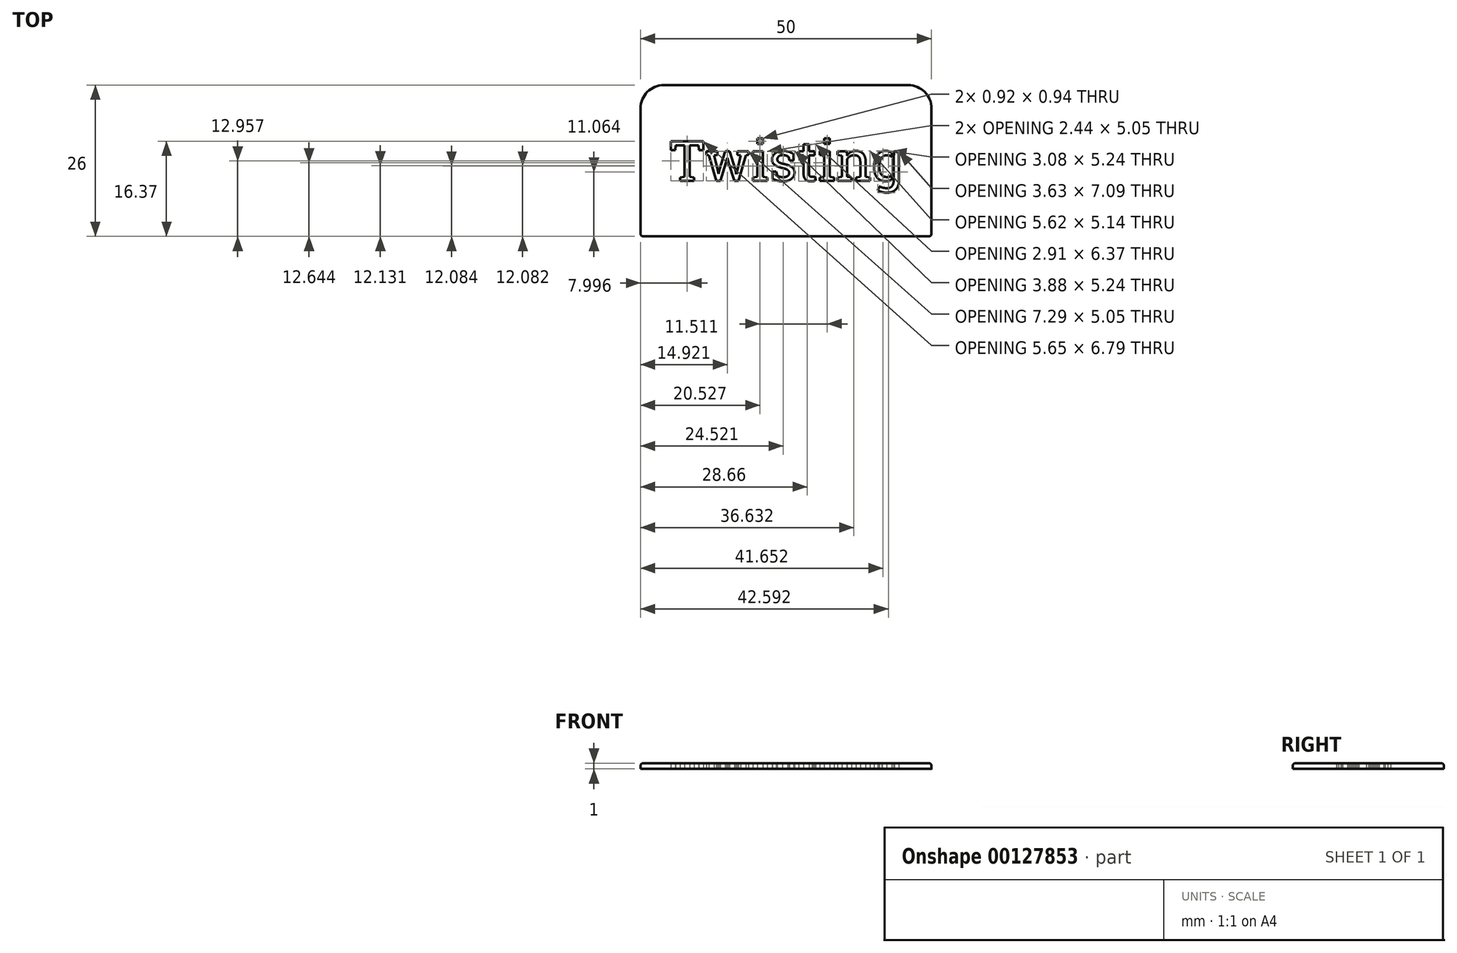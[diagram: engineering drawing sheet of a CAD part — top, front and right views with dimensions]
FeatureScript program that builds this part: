
annotation { "Feature Type Name" : "Feature", "Feature Type Description" : "" }
export const myFeature = defineFeature(function(context is Context, id is Id, definition is map)
    precondition{}
    {
        {
            var Q0;
            Q0=qCreatedBy(makeId("Top.planeOp"),FACE);
            var sketch = newSketch(context, id + "F0", { "sketchPlane" : qUnion([Q0])});
            skLineSegment(sketch, "E0.bottom", {"start": v(25, -13) * mm, "end": v(-25, -13) * mm});
            skLineSegment(sketch, "E0.top", {"start": v(21, 13) * mm, "end": v(-21, 13) * mm});
            skLineSegment(sketch, "E0.left", {"start": v(25, -13) * mm, "end": v(25, 9) * mm});
            skLineSegment(sketch, "E0.right", {"start": v(-25, -13) * mm, "end": v(-25, 9) * mm});
            skPoint(sketch, "E0.middle", {"position": v(0, 0) * mm});
            skPoint(sketch, "E1.visualSharp", {"position": v(-25, 13) * mm});
            skArc(sketch, "E1.filletArc", {"start": v(-21, 13) * mm, "mid": v(-23.83, 11.83) * mm, "end": v(-25, 9) * mm});
            skPoint(sketch, "E2.visualSharp", {"position": v(25, 13) * mm});
            skArc(sketch, "E2.filletArc", {"start": v(25, 9) * mm, "mid": v(23.83, 11.83) * mm, "end": v(21, 13) * mm});
            skText(sketch, "E3", { "text": "Twisting", "fontName": "RobotoSlab-Regular.ttf"});
            skLineSegment(sketch, "E4.bottom", {"start": v(18.5, 3.44) * mm, "end": v(18.2, 3.44) * mm});
            skLineSegment(sketch, "E4.top", {"start": v(18.5, -3.44) * mm, "end": v(18.2, -3.44) * mm});
            skLineSegment(sketch, "E4.left", {"start": v(18.5, 3.44) * mm, "end": v(18.5, -3.44) * mm});
            skLineSegment(sketch, "E4.right", {"start": v(18.2, 3.44) * mm, "end": v(18.2, -3.44) * mm});
            const initialGuessF0  = {"E3": [-0.02, -0.00344, 1, 0, 0.00688]};
            skSetInitialGuess(sketch, initialGuessF0);
            skSolve(sketch);
        }
        {
            var Q0;
            Q0=makeQuery(id+"F0.imprint","IMPRINT",FACE,{"disambiguationData":[TD([[makeQuery(id+"F0.imprint","IMPRINT",EDGE,{"derivedFrom":sQuery(id+"F0.wireOp",EDGE,"E0.bottom")}),-1.0]])]});
            var Q1;
            Q1=makeQuery(id+"F0.imprint","IMPRINT",FACE,{"disambiguationData":[TD([[makeQuery(id+"F0.imprint","IMPRINT",EDGE,{"derivedFrom":sQuery(id+"F0.wireOp",EDGE,"E3.sketch_text.stroke-172")}),1.0]])]});
            var Q2;
            {var subQ5=sQuery(id+"F0.wireOp",EDGE,"E4.bottom");Q2=makeQuery(id+"F0.imprint","IMPRINT",FACE,{"disambiguationData":[TD([[makeQuery(id+"F0.imprint","IMPRINT",EDGE,{"derivedFrom":subQ5}),1.0]])]});}
            var Q3;
            {var subQ5=sQuery(id+"F0.wireOp",EDGE,"E3.sketch_text.stroke-166");Q3=makeQuery(id+"F0.imprint","IMPRINT",FACE,{"disambiguationData":[TD([[makeQuery(id+"F0.imprint","IMPRINT",EDGE,{"derivedFrom":subQ5}),-1.0]])]});}
            var Q4;
            {var subQ0=sQuery(id+"F0.wireOp",EDGE,"E3.sketch_text.stroke-176");Q4=makeQuery(id+"F0.imprint","IMPRINT",FACE,{"disambiguationData":[TD([[makeQuery(id+"F0.imprint","IMPRINT",EDGE,{"derivedFrom":subQ0}),1.0]])]});}
            var Q5;
            {var subQ6=sQuery(id+"F0.wireOp",EDGE,"E3.sketch_text.stroke-166");Q5=makeQuery(id+"F0.imprint","IMPRINT",FACE,{"disambiguationData":[TD([[makeQuery(id+"F0.imprint","IMPRINT",EDGE,{"derivedFrom":subQ6}),1.0]])]});}
            extrude(context, id + "F1", {"entities" : qUnion([Q0, Q1, Q2, Q3, Q4, Q5]), "depth" : 1 * mm});
        }
        {
            var Q0;
            Q0=makeQuery(id+"F1.opExtrude","CAP_EDGE",EDGE,{"disambiguationData":[OSD([sQuery(id+"F0.wireOp",EDGE,"E0.right")])],"isStart":false});
            var Q1;
            Q1=makeQuery(id+"F1.opExtrude","CAP_EDGE",EDGE,{"disambiguationData":[OSD([sQuery(id+"F0.wireOp",EDGE,"E1.filletArc")])],"isStart":false});
            var Q2;
            Q2=makeQuery(id+"F1.opExtrude","CAP_EDGE",EDGE,{"disambiguationData":[OSD([sQuery(id+"F0.wireOp",EDGE,"E0.bottom")])],"isStart":false});
            var Q3;
            Q3=makeQuery(id+"F1.opExtrude","SWEPT_EDGE",EDGE,{"disambiguationData":[OSD([sQuery(id+"F0.wireOp",EDGE,"E0.bottom"),sQuery(id+"F0.wireOp",EDGE,"E0.left")])]});
            var Q4;
            Q4=makeQuery(id+"F1.opExtrude","SWEPT_EDGE",EDGE,{"disambiguationData":[OSD([sQuery(id+"F0.wireOp",EDGE,"E0.bottom"),sQuery(id+"F0.wireOp",EDGE,"E0.right")])]});
            fillet(context, id + "F2", {"entities" : qUnion([Q0, Q1, Q2, Q3, Q4]), "radius" : .5 * mm, "tangentPropagation" : true, "allowEdgeOverflow" : false});
        }
    });
